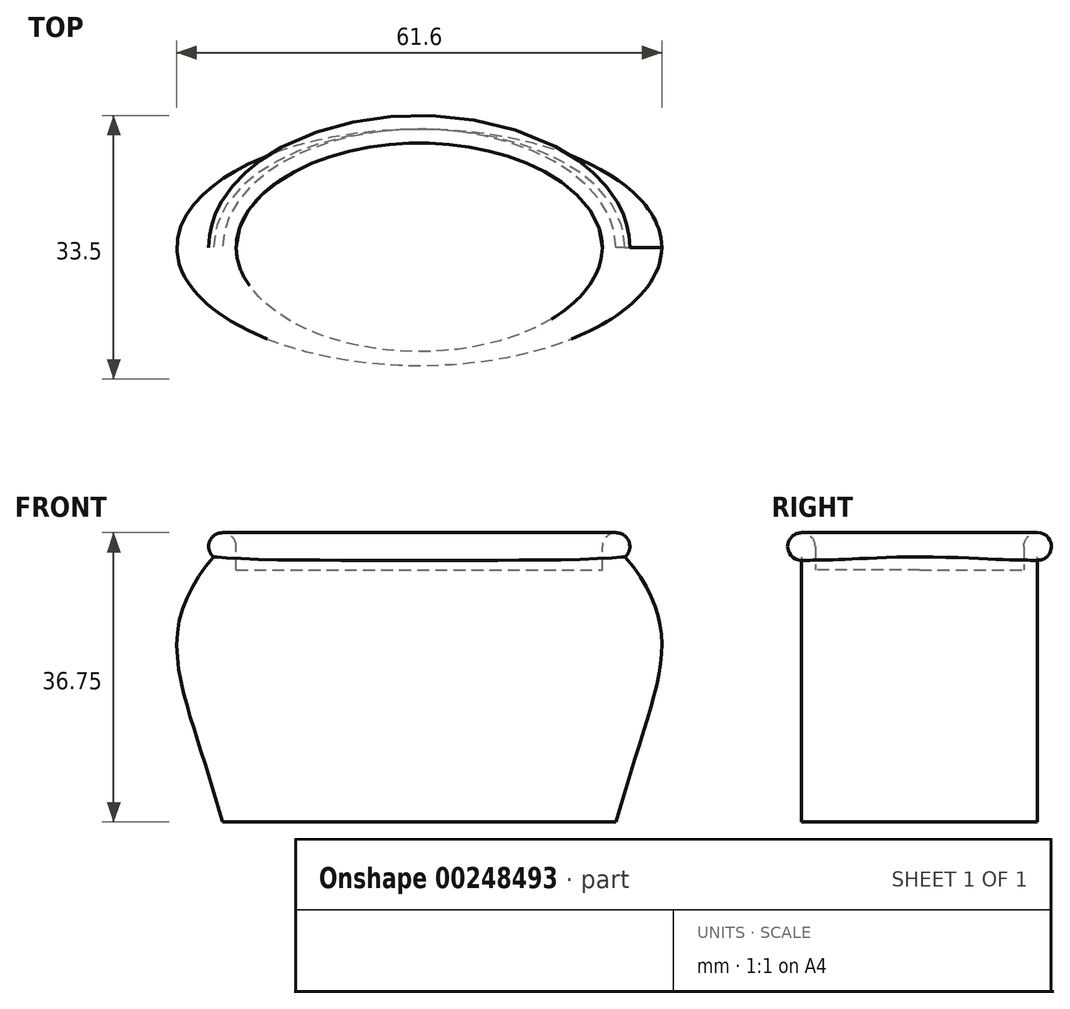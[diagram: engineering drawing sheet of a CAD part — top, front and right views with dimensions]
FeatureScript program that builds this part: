
annotation { "Feature Type Name" : "Feature", "Feature Type Description" : "" }
export const myFeature = defineFeature(function(context is Context, id is Id, definition is map)
    precondition{}
    {
        {
            var Q0;
            Q0=qCreatedBy(makeId("Top.planeOp"),FACE);
            var sketch = newSketch(context, id + "F0", { "sketchPlane" : qUnion([Q0])});
            skEllipse(sketch, "E0", {"center": v(0, 0) * mm, "majorRadius": 25 * mm, "minorRadius": 15 * mm, "majorAxis": v(1, 0)});
            skSolve(sketch);
        }
        {
            var Q0;
            Q0=qCreatedBy(makeId("Top.planeOp"),FACE);
            cPlane(context, id + "F1", {"entities" : qUnion([Q0]), "cplaneType" : CPlaneType.OFFSET, "offset" : 35 * mm, "width" : 150 * mm, "height" : 150 * mm});
        }
        {
            var Q0;
            Q0=qCreatedBy(id+"F1.planeOp",FACE);
            var sketch = newSketch(context, id + "F2", { "sketchPlane" : qUnion([Q0])});
            skEllipse(sketch, "E1.0", {"center": v(0, 0) * mm, "majorRadius": 25 * mm, "minorRadius": 15 * mm, "majorAxis": v(1, 0)});
            skSolve(sketch);
        }
        {
            var Q0;
            Q0=qCreatedBy(makeId("Front.planeOp"),FACE);
            var sketch = newSketch(context, id + "F3", { "sketchPlane" : qUnion([Q0])});
            skFitSpline(sketch, "E2.0", {"points": [v(25, 35) * mm, v(8.33, 35) * mm, v(-8.33, 35) * mm, v(-25, 35) * mm]});
            skFitSpline(sketch, "E3", {"points": [v(25, 35) * mm, v(25, 0) * mm], "startDerivative": vector(30.3, -33.05) * mm, "endDerivative": vector(-14.84, -53.71) * mm});
            skFitSpline(sketch, "E4.MirrorCS", {"points": [v(-25, 35) * mm, v(-25, 0) * mm], "startDerivative": vector(-30.3, -33.05) * mm, "endDerivative": vector(14.84, -53.71) * mm});
            skSolve(sketch);
        }
        {
            var Q0;
            Q0=makeQuery(id+"F2.imprint","IMPRINT",FACE,{"disambiguationData":[TD([[makeQuery(id+"F2.imprint","IMPRINT",EDGE,{"derivedFrom":sQuery(id+"F2.wireOp",EDGE,"E1.0")}),1.0]])]});
            var Q1;
            Q1=makeQuery(id+"F0.imprint","IMPRINT",FACE,{"disambiguationData":[TD([[makeQuery(id+"F0.imprint","IMPRINT",EDGE,{"derivedFrom":sQuery(id+"F0.wireOp",EDGE,"E0")}),1.0]])]});
            var Q2;
            Q2=sQuery(id+"F3.wireOp",EDGE,"E3");
            var Q3;
            Q3=sQuery(id+"F3.wireOp",EDGE,"E4.MirrorCS");
            loft(context, id + "F4", {"addGuides" : true, "sheetProfilesArray" : [{ "sheetProfileEntities" : qUnion([Q0]) }, { "sheetProfileEntities" : qUnion([Q1]) }], "guidesArray" : [{ "guideEntities" : qUnion([Q2]), "guideDerivativeType" : LoftGuideDerivativeType.DEFAULT, "guideDerivativeMagnitude" : 1 }, { "guideEntities" : qUnion([Q3]), "guideDerivativeType" : LoftGuideDerivativeType.DEFAULT, "guideDerivativeMagnitude" : 1 }]});
        }
        {
            var Q0;
            Q0=qCreatedBy(makeId("Front.planeOp"),FACE);
            var sketch = newSketch(context, id + "F5", { "sketchPlane" : qUnion([Q0])});
            skPoint(sketch, "E5.0", {"position": v(-25, 35) * mm});
            skCircle(sketch, "E6", {"center": v(-25, 35) * mm, "radius": 1.75 * mm});
            skSolve(sketch);
        }
        {
            var Q0;
            Q0=makeQuery(id+"F5.imprint","IMPRINT",FACE,{"disambiguationData":[TD([[makeQuery(id+"F5.imprint","IMPRINT",EDGE,{"derivedFrom":sQuery(id+"F5.wireOp",EDGE,"E6")}),1.0]])]});
            var Q1;
            Q1=makeQuery(id+"F4.opLoft","MID_CAP_EDGE",EDGE,{"disambiguationData":[OSD([sQuery(id+"F2.wireOp",EDGE,"E1.0"),sQuery(id+"F3.wireOp",EDGE,"E3"),sQuery(id+"F3.wireOp",EDGE,"E4.MirrorCS")]),OD(0.0)],"capPos":0.0});
            var Q2;
            Q2=makeQuery(id+"F4.opLoft","MID_CAP_EDGE",EDGE,{"disambiguationData":[OSD([sQuery(id+"F2.wireOp",EDGE,"E1.0"),sQuery(id+"F3.wireOp",EDGE,"E3"),sQuery(id+"F3.wireOp",EDGE,"E4.MirrorCS")]),OD(1.0)],"capPos":0.0});
            sweep(context, id + "F6", {"operationType" : NewBodyOperationType.ADD, "profiles" : qUnion([Q0]), "path" : qUnion([Q1, Q2])});
        }
        {
            var Q0;
            Q0=makeQuery(id+"F4.opLoft","CAP_FACE",FACE,{"disambiguationData":[OSD([makeQuery(id+"F2.imprint","IMPRINT",FACE,{"disambiguationData":[TD([[makeQuery(id+"F2.imprint","IMPRINT",EDGE,{"derivedFrom":sQuery(id+"F2.wireOp",EDGE,"E1.0")}),1.0]])]})])],"isStart":true});
            extrude(context, id + "F7", {"entities" : qUnion([Q0]), "operationType" : NewBodyOperationType.REMOVE, "oppositeDirection" : true, "depth" : 3 * mm});
        }
    });
